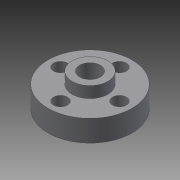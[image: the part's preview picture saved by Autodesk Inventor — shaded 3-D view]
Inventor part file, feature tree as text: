
AUTODESK INVENTOR PART (.ipt)
format: ipt  version: 2015 (Build 190159000, 159)  size: 102,912 bytes
history: native  units: in
note: dims shown in document units (in); Inventor stores cm internally (conversion verified against a paired STEP export)
features: sketch x2, hole x2, revolve x1
ambient origin geometry x8: Origin, YZ Plane, XZ Plane, XY Plane, X Axis, Y Axis, Z Axis, Center Point
bodies: Solid1 (feature_tree)
feature tree (5):
  revolve  "Revolution1"  [1 undecoded]
  sketch  "Sketch3"  dims[d2=0.8in d3=0.34in d4=90.0deg d23=1.125in d24=1.125in d25=0.3937in d26=0.75in d27=0.375in d28=0.25in d29=0.5635in d30=1.0in d31=0.8108in d32=0.266in d33=0.75in d34=0.375in d35=0.25in d36=0.5635in d37=1.0in d38=0.8108in]
  hole  "Hole3"  [1 undecoded]
  hole  "Hole4"  [1 undecoded]
  sketch  "Sketch1"  dims[d0=0.625in d1=0.41in]
note: 3 required parameter values undecoded (feature->parameter linkage not recoverable at this tier; creation-order binding heuristic only, values carry confidence <= 0.55)